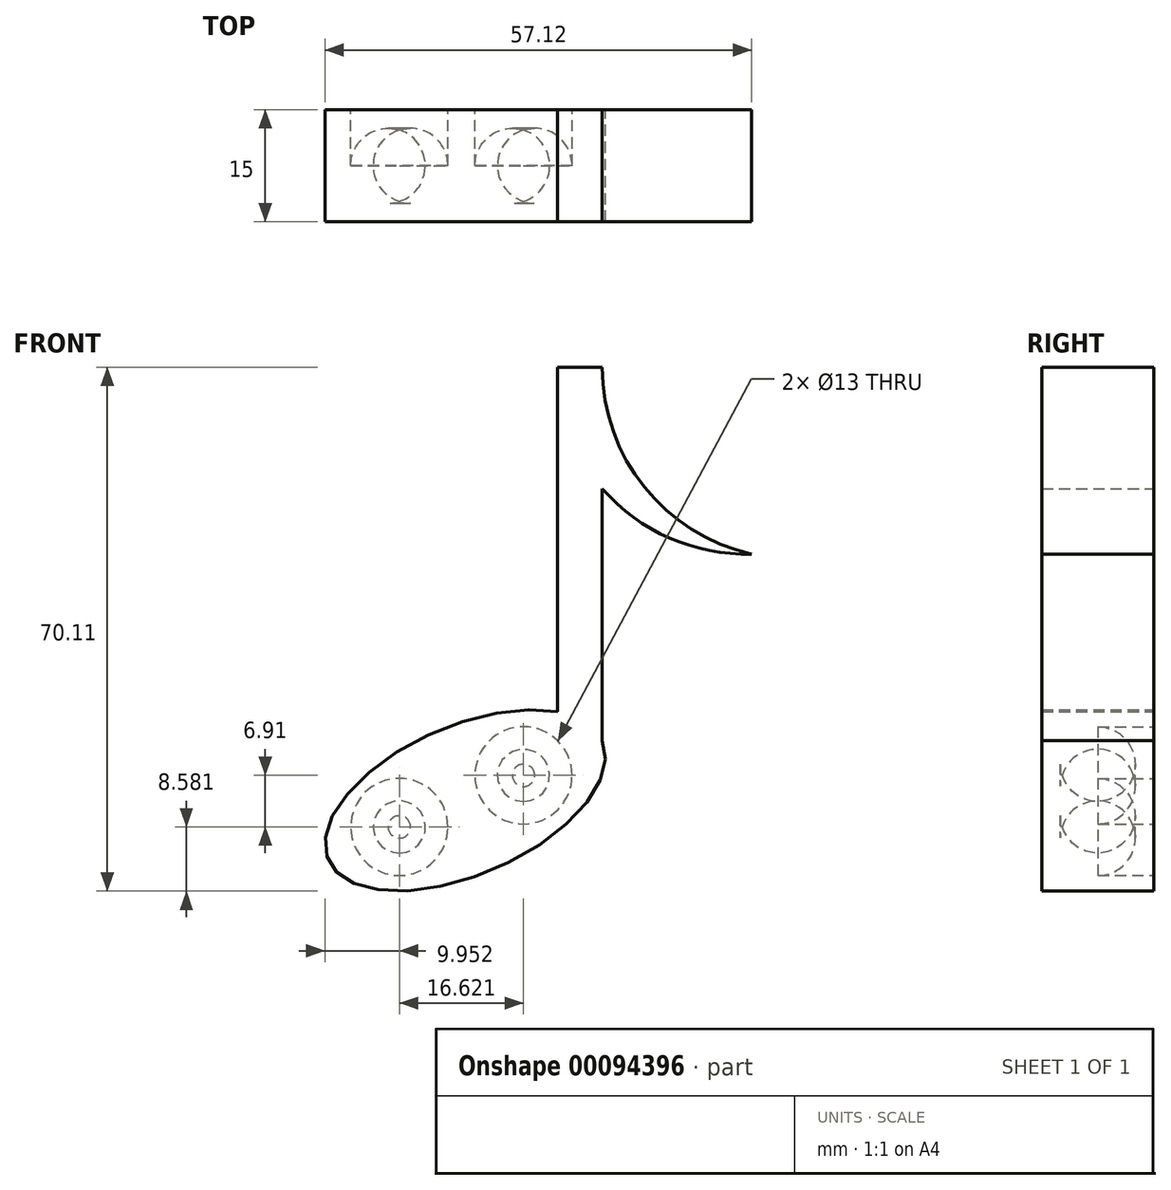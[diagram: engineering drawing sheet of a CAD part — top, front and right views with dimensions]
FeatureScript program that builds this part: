
annotation { "Feature Type Name" : "Feature", "Feature Type Description" : "" }
export const myFeature = defineFeature(function(context is Context, id is Id, definition is map)
    precondition{}
    {
        {
            var Q0;
            Q0=qCreatedBy(makeId("Front.planeOp"),FACE);
            var sketch = newSketch(context, id + "F0", { "sketchPlane" : qUnion([Q0])});
            skEllipse(sketch, "E0", {"center": v(0, 0) * mm, "majorRadius": 20 * mm, "minorRadius": 10 * mm, "majorAxis": v(-0.92, -0.4)});
            skLineSegment(sketch, "E1.bottom", {"start": v(18.35, 7.96) * mm, "end": v(12.35, 7.96) * mm});
            skLineSegment(sketch, "E1.top", {"start": v(18.35, 57.96) * mm, "end": v(12.35, 57.96) * mm});
            skLineSegment(sketch, "E1.left", {"start": v(18.35, 7.96) * mm, "end": v(18.35, 57.96) * mm});
            skLineSegment(sketch, "E1.right", {"start": v(12.35, 7.96) * mm, "end": v(12.35, 57.96) * mm});
            skLineSegment(sketch, "E2", {"start": v(15.35, 57.96) * mm, "end": v(15.35, 32.96) * mm, "construction": true});
            skPoint(sketch, "E3.endSnap0", {"position": v(18.35, 32.96) * mm});
            skLineSegment(sketch, "E4", {"start": v(15.35, 32.96) * mm, "end": v(58.24, 32.96) * mm, "construction": true});
            skArc(sketch, "E5", {"start": v(18.35, 57.96) * mm, "mid": v(23.96, 41.96) * mm, "end": v(38.35, 32.96) * mm});
            skArc(sketch, "E6", {"start": v(18.35, 41.7) * mm, "mid": v(27.37, 35.1) * mm, "end": v(38.35, 32.96) * mm});
            skSolve(sketch);
        }
        {
            var Q0;
            {var subQ0=sQuery(id+"F0.wireOp",EDGE,"E1.bottom");Q0=makeQuery(id+"F0.imprint","IMPRINT",FACE,{"disambiguationData":[TD([[makeQuery(id+"F0.imprint","IMPRINT",EDGE,{"derivedFrom":subQ0}),1.0]])]});}
            var Q1;
            {var subQ0=sQuery(id+"F0.wireOp",EDGE,"E1.bottom");Q1=makeQuery(id+"F0.imprint","IMPRINT",FACE,{"disambiguationData":[TD([[makeQuery(id+"F0.imprint","IMPRINT",EDGE,{"derivedFrom":subQ0}),-1.0]])]});}
            var Q2;
            {var subQ1=sQuery(id+"F0.wireOp",EDGE,"E0");var subQ3=sQuery(id+"F0.wireOp",EDGE,"E1.right");var subQ4=makeQuery(id+"F0.imprint","INTERSECT",VERTEX,{"derivedFrom":[subQ1,subQ3]});Q2=makeQuery(id+"F0.imprint","IMPRINT",FACE,{"disambiguationData":[TD([[makeQuery(id+"F0.imprint","IMPRINT",EDGE,{"disambiguationData":[TD([[subQ4,1.0]])],"derivedFrom":subQ1}),-1.0]])]});}
            var Q3;
            {var subQ0=sQuery(id+"F0.wireOp",EDGE,"E1.top");Q3=makeQuery(id+"F0.imprint","IMPRINT",FACE,{"disambiguationData":[TD([[makeQuery(id+"F0.imprint","IMPRINT",EDGE,{"derivedFrom":subQ0}),1.0]])]});}
            extrude(context, id + "F1", {"entities" : qUnion([Q0, Q1, Q2, Q3]), "depth" : 15 * mm});
        }
        {
            var Q0;
            {var subQ0=sQuery(id+"F0.wireOp",EDGE,"E5");Q0=makeQuery(id+"F0.imprint","IMPRINT",FACE,{"disambiguationData":[TD([[makeQuery(id+"F0.imprint","IMPRINT",EDGE,{"derivedFrom":subQ0}),-1.0]])]});}
            extrude(context, id + "F2", {"entities" : qUnion([Q0]), "depth" : 15 * mm});
        }
        {
            var Q0;
            Q0=makeQuery(id+"F1.opExtrude","SWEPT_BODY",BODY,{"disambiguationData":[OSD([sQuery(id+"F0.wireOp",EDGE,"E0"),sQuery(id+"F0.wireOp",EDGE,"E1.top"),sQuery(id+"F0.wireOp",EDGE,"E1.left"),sQuery(id+"F0.wireOp",EDGE,"E1.right")])]});
            var Q1;
            Q1=makeQuery(id+"F2.opExtrude","SWEPT_BODY",BODY,{"disambiguationData":[OSD([sQuery(id+"F0.wireOp",EDGE,"E1.left"),sQuery(id+"F0.wireOp",EDGE,"E5"),sQuery(id+"F0.wireOp",EDGE,"E6")])]});
            booleanBodies(context, id + "F3", {"operationType" : BooleanOperationType.UNION, "tools" : qUnion([Q0, Q1])});
        }
        {
            var Q0;
            {var subQ0=sQuery(id+"F0.wireOp",EDGE,"E1.left");Q0=makeQuery(id+"F3.opBoolean","MERGE",FACE,{"derivedFrom":[makeQuery(id+"F1.opExtrude","CAP_FACE",FACE,{"disambiguationData":[OSD([sQuery(id+"F0.wireOp",EDGE,"E0"),sQuery(id+"F0.wireOp",EDGE,"E1.top"),subQ0,sQuery(id+"F0.wireOp",EDGE,"E1.right")])],"isStart":true}),makeQuery(id+"F2.opExtrude","CAP_FACE",FACE,{"disambiguationData":[OSD([subQ0,sQuery(id+"F0.wireOp",EDGE,"E5"),sQuery(id+"F0.wireOp",EDGE,"E6")])],"isStart":true})]});}
            var sketch = newSketch(context, id + "F4", { "sketchPlane" : qUnion([Q0])});
            skCircle(sketch, "E7", {"center": v(-7.8, 3.34) * mm, "radius": 6.5 * mm});
            skCircle(sketch, "E8", {"center": v(8.82, -3.57) * mm, "radius": 6.5 * mm});
            skSolve(sketch);
        }
        {
            var Q0;
            Q0=makeQuery(id+"F4.imprint","IMPRINT",FACE,{"disambiguationData":[TD([[makeQuery(id+"F4.imprint","IMPRINT",EDGE,{"derivedFrom":sQuery(id+"F4.wireOp",EDGE,"E7")}),1.0]])]});
            var Q1;
            Q1=makeQuery(id+"F4.imprint","IMPRINT",FACE,{"disambiguationData":[TD([[makeQuery(id+"F4.imprint","IMPRINT",EDGE,{"derivedFrom":sQuery(id+"F4.wireOp",EDGE,"E8")}),1.0]])]});
            extrude(context, id + "F5", {"entities" : qUnion([Q0, Q1]), "operationType" : NewBodyOperationType.REMOVE, "oppositeDirection" : true, "depth" : 12.5 * mm});
        }
        {
            var Q0;
            Q0=makeQuery(id+"F5.boolean.opBoolean","COPY",EDGE,{"derivedFrom":makeQuery(id+"F5.opExtrude","CAP_EDGE",EDGE,{"disambiguationData":[OSD([sQuery(id+"F4.wireOp",EDGE,"E8")])],"isStart":false})});
            var Q1;
            Q1=makeQuery(id+"F5.boolean.opBoolean","COPY",EDGE,{"derivedFrom":makeQuery(id+"F5.opExtrude","CAP_EDGE",EDGE,{"disambiguationData":[OSD([sQuery(id+"F4.wireOp",EDGE,"E7")])],"isStart":false})});
            fillet(context, id + "F6", {"entities" : qUnion([Q0, Q1]), "radius" : 5 * mm, "tangentPropagation" : true, "allowEdgeOverflow" : false});
        }
    });
